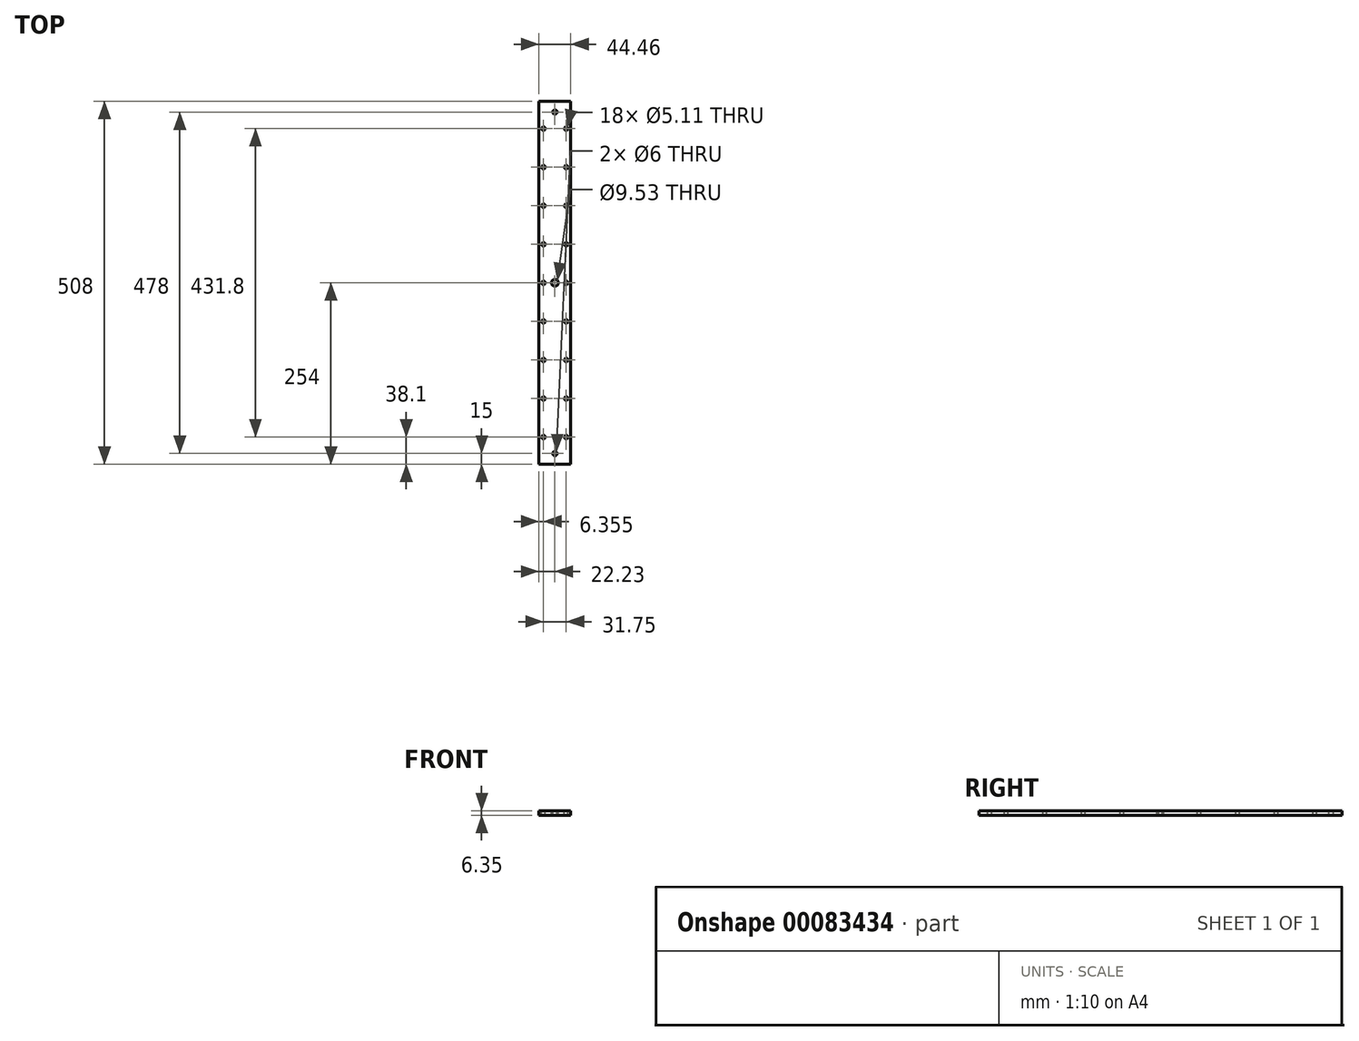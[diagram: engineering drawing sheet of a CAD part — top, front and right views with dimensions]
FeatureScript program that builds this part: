
annotation { "Feature Type Name" : "Feature", "Feature Type Description" : "" }
export const myFeature = defineFeature(function(context is Context, id is Id, definition is map)
    precondition{}
    {
        {
            var Q0;
            Q0=qCreatedBy(makeId("Top.planeOp"),FACE);
            var sketch = newSketch(context, id + "F0", { "sketchPlane" : qUnion([Q0])});
            skLineSegment(sketch, "E0.bottom", {"start": v(-22.23, -254) * mm, "end": v(22.22, -254) * mm});
            skLineSegment(sketch, "E0.top", {"start": v(-22.23, 254) * mm, "end": v(22.22, 254) * mm});
            skLineSegment(sketch, "E0.left", {"start": v(-22.23, -254) * mm, "end": v(-22.23, 254) * mm});
            skLineSegment(sketch, "E0.right", {"start": v(22.22, -254) * mm, "end": v(22.22, 254) * mm});
            skPoint(sketch, "E0.middle", {"position": v(0, 0) * mm});
            skSolve(sketch);
        }
        {
            var Q0;
            Q0 = qSketchRegion(id + "F0", true);
            extrude(context, id + "F1", {"entities" : qUnion([Q0]), "depth" : 6.35 * mm});
        }
        {
            var Q0;
            Q0=makeQuery(id+"F1.opExtrude","CAP_FACE",FACE,{"disambiguationData":[OSD([sQuery(id+"F0.wireOp",EDGE,"E0.bottom"),sQuery(id+"F0.wireOp",EDGE,"E0.top"),sQuery(id+"F0.wireOp",EDGE,"E0.left"),sQuery(id+"F0.wireOp",EDGE,"E0.right")])],"isStart":false});
            var sketch = newSketch(context, id + "F2", { "sketchPlane" : qUnion([Q0])});
            skLineSegment(sketch, "E1", {"start": v(-22.23, 0) * mm, "end": v(22.23, 0) * mm, "construction": true});
            skPoint(sketch, "E2", {"position": v(-15.88, 0) * mm});
            skPoint(sketch, "E3", {"position": v(15.88, 0) * mm});
            skPoint(sketch, "E4.0.1.0", {"position": v(15.88, 53.97) * mm});
            skPoint(sketch, "E4.0.1.1", {"position": v(-15.88, 53.97) * mm});
            skPoint(sketch, "E4.0.2.0", {"position": v(15.88, 107.95) * mm});
            skPoint(sketch, "E4.0.2.1", {"position": v(-15.88, 107.95) * mm});
            skPoint(sketch, "E4.0.3.0", {"position": v(15.88, 161.92) * mm});
            skPoint(sketch, "E4.0.3.1", {"position": v(-15.88, 161.92) * mm});
            skPoint(sketch, "E4.0.4.0", {"position": v(15.88, 215.9) * mm});
            skPoint(sketch, "E4.0.4.1", {"position": v(-15.88, 215.9) * mm});
            skLineSegment(sketch, "E4.direction1", {"start": v(15.88, 0) * mm, "end": v(22.23, 0) * mm, "construction": true});
            skLineSegment(sketch, "E4.direction2", {"start": v(15.88, 0) * mm, "end": v(15.88, 53.97) * mm, "construction": true});
            skPoint(sketch, "E5.0.1.0", {"position": v(-15.88, -53.97) * mm});
            skPoint(sketch, "E5.0.1.1", {"position": v(15.87, -53.97) * mm});
            skPoint(sketch, "E5.0.2.0", {"position": v(-15.88, -107.95) * mm});
            skPoint(sketch, "E5.0.2.1", {"position": v(15.87, -107.95) * mm});
            skPoint(sketch, "E5.0.3.0", {"position": v(-15.88, -161.92) * mm});
            skPoint(sketch, "E5.0.3.1", {"position": v(15.87, -161.92) * mm});
            skPoint(sketch, "E5.0.4.0", {"position": v(-15.88, -215.9) * mm});
            skPoint(sketch, "E5.0.4.1", {"position": v(15.87, -215.9) * mm});
            skLineSegment(sketch, "E5.direction1", {"start": v(-15.88, 0) * mm, "end": v(9.53, 0) * mm, "construction": true});
            skLineSegment(sketch, "E5.direction2", {"start": v(-15.88, 0) * mm, "end": v(-15.88, -53.97) * mm, "construction": true});
            skSolve(sketch);
        }
        {
            var Q0;
            Q0=sQuery(id+"F2.wireOp",VERTEX,"E5.0.4.0");
            var Q1;
            Q1=sQuery(id+"F2.wireOp",VERTEX,"E5.0.4.1");
            var Q2;
            Q2=sQuery(id+"F2.wireOp",VERTEX,"E5.0.3.1");
            var Q3;
            Q3=sQuery(id+"F2.wireOp",VERTEX,"E5.0.3.0");
            var Q4;
            Q4=sQuery(id+"F2.wireOp",VERTEX,"E5.0.2.0");
            var Q5;
            Q5=sQuery(id+"F2.wireOp",VERTEX,"E5.0.2.1");
            var Q6;
            Q6=sQuery(id+"F2.wireOp",VERTEX,"E5.0.1.1");
            var Q7;
            Q7=sQuery(id+"F2.wireOp",VERTEX,"E5.0.1.0");
            var Q8;
            Q8=sQuery(id+"F2.wireOp",VERTEX,"E2");
            var Q9;
            Q9=sQuery(id+"F2.wireOp",VERTEX,"E3");
            var Q10;
            Q10=sQuery(id+"F2.wireOp",VERTEX,"E4.0.1.0");
            var Q11;
            Q11=sQuery(id+"F2.wireOp",VERTEX,"E4.0.1.1");
            var Q12;
            Q12=sQuery(id+"F2.wireOp",VERTEX,"E4.0.2.1");
            var Q13;
            Q13=sQuery(id+"F2.wireOp",VERTEX,"E4.0.2.0");
            var Q14;
            Q14=sQuery(id+"F2.wireOp",VERTEX,"E4.0.3.1");
            var Q15;
            Q15=sQuery(id+"F2.wireOp",VERTEX,"E4.0.3.0");
            var Q16;
            Q16=sQuery(id+"F2.wireOp",VERTEX,"E4.0.4.0");
            var Q17;
            Q17=sQuery(id+"F2.wireOp",VERTEX,"E4.0.4.1");
            var Q18;
            Q18=makeQuery(id+"F1.opExtrude","SWEPT_BODY",BODY,{"disambiguationData":[OSD([sQuery(id+"F0.wireOp",EDGE,"E0.bottom"),sQuery(id+"F0.wireOp",EDGE,"E0.top"),sQuery(id+"F0.wireOp",EDGE,"E0.left"),sQuery(id+"F0.wireOp",EDGE,"E0.right")])]});
            hole(context, id + "F3", {"style" : HoleStyle.SIMPLE, "endStyle" : HoleEndStyle.THROUGH, "standardTappedOrClearance" : lookupTablePath({ "standard" : "ANSI", "fit" : "Normal (ASME)", "size" : "#10", "type" : "Clearance" }), "standardBlindInLast" : lookupTablePath({ "fit" : "Free", "standard" : "ANSI", "size" : "#10", "type" : "Clearance" }), "holeDiameter" : 5.1 * mm, "locations" : qUnion([Q0, Q1, Q2, Q3, Q4, Q5, Q6, Q7, Q8, Q9, Q10, Q11, Q12, Q13, Q14, Q15, Q16, Q17]), "scope" : qUnion([Q18]), "isTappedThrough" : true});
        }
        {
            var Q0;
            Q0=makeQuery(id+"F1.opExtrude","CAP_FACE",FACE,{"disambiguationData":[OSD([sQuery(id+"F0.wireOp",EDGE,"E0.bottom"),sQuery(id+"F0.wireOp",EDGE,"E0.top"),sQuery(id+"F0.wireOp",EDGE,"E0.left"),sQuery(id+"F0.wireOp",EDGE,"E0.right")])],"isStart":false});
            var sketch = newSketch(context, id + "F4", { "sketchPlane" : qUnion([Q0])});
            skLineSegment(sketch, "E6", {"start": v(0, -254) * mm, "end": v(0, 254) * mm, "construction": true});
            skCircle(sketch, "E7", {"center": v(0, -239) * mm, "radius": 3 * mm});
            skCircle(sketch, "E8", {"center": v(0, 239) * mm, "radius": 3 * mm});
            skSolve(sketch);
        }
        {
            var Q0;
            Q0 = qSketchRegion(id + "F4", true);
            extrude(context, id + "F5", {"entities" : qUnion([Q0]), "operationType" : NewBodyOperationType.REMOVE, "endBound" : BoundingType.UP_TO_NEXT, "oppositeDirection" : true, "depth" : 25.4 * mm});
        }
        {
            var Q0;
            Q0=makeQuery(id+"F1.opExtrude","CAP_FACE",FACE,{"disambiguationData":[OSD([sQuery(id+"F0.wireOp",EDGE,"E0.bottom"),sQuery(id+"F0.wireOp",EDGE,"E0.top"),sQuery(id+"F0.wireOp",EDGE,"E0.left"),sQuery(id+"F0.wireOp",EDGE,"E0.right")])],"isStart":false});
            var sketch = newSketch(context, id + "F6", { "sketchPlane" : qUnion([Q0])});
            skCircle(sketch, "E9", {"center": v(0, 0) * mm, "radius": 4.76 * mm});
            skSolve(sketch);
        }
        {
            var Q0;
            Q0 = qSketchRegion(id + "F6", true);
            extrude(context, id + "F7", {"entities" : qUnion([Q0]), "operationType" : NewBodyOperationType.REMOVE, "endBound" : BoundingType.UP_TO_NEXT, "oppositeDirection" : true, "depth" : 25.4 * mm});
        }
    });
